# Revit family: Toilet_Universal-Floor_Mount-Sloan-ST-2309
name_source: partatom
category: Plumbing Fixtures
revit_build: Autodesk Revit 2014 (Build: 20130308_1515(x64)
units: mm (PartAtom-declared; Revit-internal decimal feet)

## types (1)
- ST-2309
    ADA Compliant = Yes
    Assembly Code = D2010110
    CW Connection = Yes
    CWFU = 10
    Default Elevation = 0"
    Description = Complete vitreous china water closet.
    Fixture Color = White
    Fixture Material = Vitreous China-Sloan-White
    Flush Choice = Single Flush
    Flush Volume = 1.1 to 1.6 gpf/(4.2 to 6.0 Lpf)
    HW Connection = No
    HWFU = 0
    Height = 10 3/4"
    IAPMO Compliance = cUPC
    Inlet Spud Size = 1-1/2" I.P.S.
    Length = 27"
    Manufacturer = SLOAN
    Model = ST-2309
    Mounting = Floor Mounted
    Order Code = 2102309
    Price = Prices may vary. Please consult Manufacturer Representative for most up-to-date price list.
    Product Documentation Link = https://specifications.sloan.com
    Product Page URL = https://www.sloan.com
    Rough-in = 10"
    Spud Location = Top Spud
    URL = https://www.sloan.com
    Vent Connection = No
    WFU = 10
    Waste Connection = Yes
    Waste Connection Diameter = 2 1/4"
    Waste Connection Radius = 1"
    Width = 13"

## geometry (parser evidence)
native form markers: Sweep x1
no freeform markers — native parametric forms only
